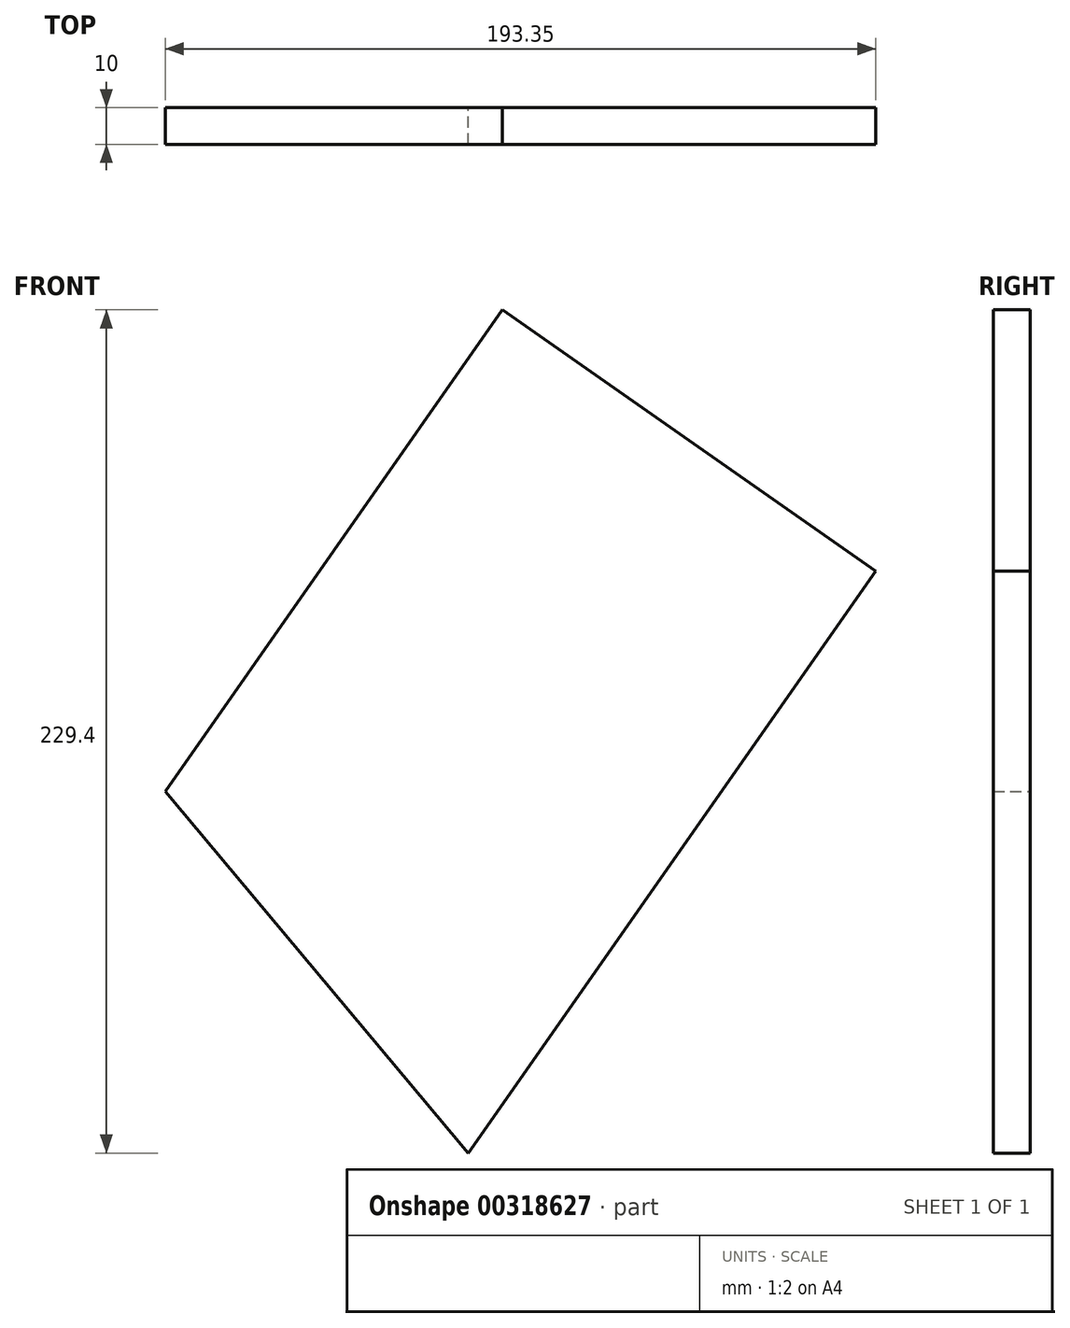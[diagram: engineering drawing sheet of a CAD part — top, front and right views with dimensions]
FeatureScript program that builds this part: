
annotation { "Feature Type Name" : "Feature", "Feature Type Description" : "" }
export const myFeature = defineFeature(function(context is Context, id is Id, definition is map)
    precondition{}
    {
        {
            var Q0;
            Q0=qCreatedBy(makeId("Front.planeOp"),FACE);
            var sketch = newSketch(context, id + "F0", { "sketchPlane" : qUnion([Q0])});
            skLineSegment(sketch, "E0", {"start": v(8.25, 0) * mm, "end": v(162.1, 0) * mm, "construction": true});
            skLineSegment(sketch, "E1", {"start": v(0, 0) * mm, "end": v(110.83, 158.28) * mm});
            skLineSegment(sketch, "E2", {"start": v(110.83, 158.28) * mm, "end": v(9.25, 229.4) * mm});
            skLineSegment(sketch, "E3", {"start": v(9.25, 229.4) * mm, "end": v(-82.52, 98.34) * mm});
            skLineSegment(sketch, "E4", {"start": v(-82.52, 98.34) * mm, "end": v(0, 0) * mm});
            skSolve(sketch);
        }
        {
            var Q0;
            Q0=makeQuery(id+"F0.imprint","IMPRINT",FACE,{"disambiguationData":[TD([[makeQuery(id+"F0.imprint","IMPRINT",EDGE,{"derivedFrom":sQuery(id+"F0.wireOp",EDGE,"E1")}),1.0]])]});
            extrude(context, id + "F1", {"entities" : qUnion([Q0]), "depth" : 10 * mm});
        }
    });
